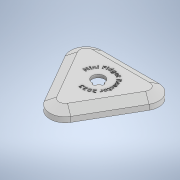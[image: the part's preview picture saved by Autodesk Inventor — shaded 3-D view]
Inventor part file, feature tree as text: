
AUTODESK INVENTOR PART (.ipt)
format: ipt  version: 2022.4 (Build 264492010, 492A)  size: 798,208 bytes
history: native  units: mm
features: sketch x4, extrude x3, chamfer x2, emboss x1
ambient origin geometry x8: Origin, YZ Plane, XZ Plane, XY Plane, X Axis, Y Axis, Z Axis, Center Point
bodies: Solid1 (feature_tree)
feature tree (10):
  extrude  "Extrusion1"  Depth=93.530744mm
  extrude  "Extrusion2"  Depth=60.0mm
  chamfer  "Chamfer3"  Distance=5.0mm
  extrude  "Extrusion3"  Depth=1.0mm
  emboss  "Emboss1"
  chamfer  "Chamfer4"  Distance=20.0mm
  sketch  "Sketch1"  dims[d0=93.530744mm d1=93.530744mm]
  sketch  "Sketch2"  dims[d2=93.530744mm d3=60.0mm]
  sketch  "Sketch3"  dims[d4=15.0mm d5=5.0mm d6=0.0mm]
  sketch  "Sketch4"  dims[d7=93.530744mm d8=93.530744mm d9=93.530744mm d10=60.0mm d11=15.0mm d12=12.0mm d13=0.0mm d20=12.5mm d21=2.0mm d22=5.585054mm d23=20.0mm d24=6.0mm d25=6.0mm d26=0.0mm d27=0.0mm d28=1.0mm d29=0.0mm d30=14.75mm d31=2.0mm d32=30.0deg d34=37.0mm d35=37.0mm d36=37.0mm d37=1.0mm d38=1.0mm d39=0.5mm d40=0.872665mm d41=0.5mm d42=0.872665mm]
